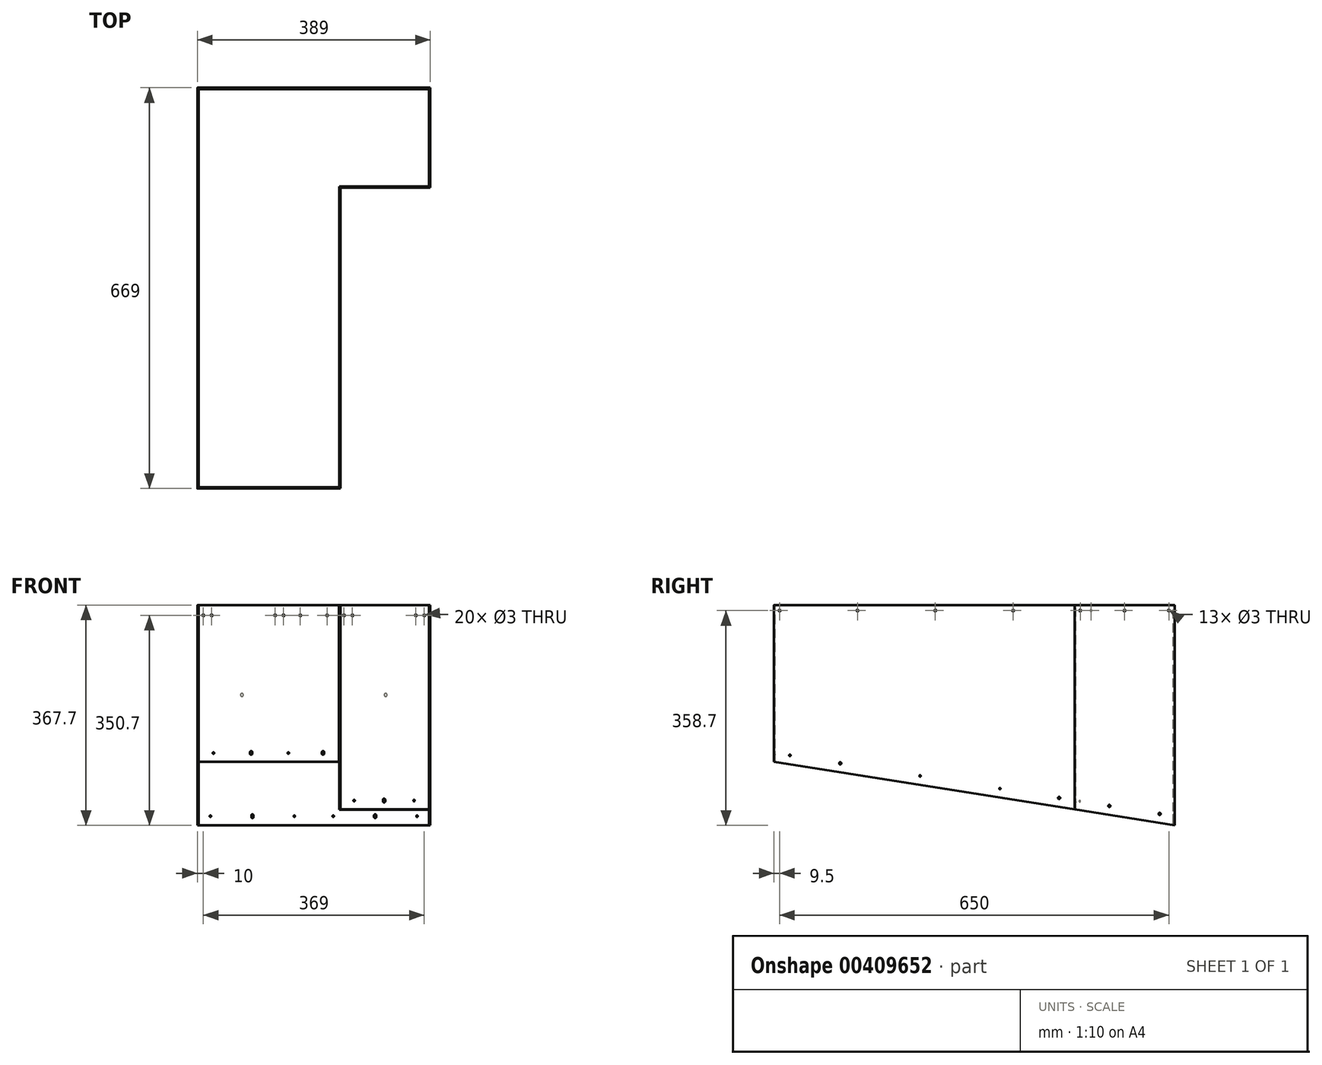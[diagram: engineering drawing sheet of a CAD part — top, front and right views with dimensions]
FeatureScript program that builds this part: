
annotation { "Feature Type Name" : "Feature", "Feature Type Description" : "" }
export const myFeature = defineFeature(function(context is Context, id is Id, definition is map)
    precondition{}
    {
        {
            var Q0;
            Q0=qCreatedBy(makeId("Top.planeOp"),FACE);
            var sketch = newSketch(context, id + "F0", { "sketchPlane" : qUnion([Q0])});
            skLineSegment(sketch, "E0.bottom", {"start": v(192.25, 332.5) * mm, "end": v(-192.25, 332.5) * mm});
            skLineSegment(sketch, "E0.top", {"start": v(192.25, 334.5) * mm, "end": v(-192.25, 334.5) * mm});
            skLineSegment(sketch, "E0.left", {"start": v(192.25, 332.5) * mm, "end": v(192.25, 334.5) * mm});
            skLineSegment(sketch, "E0.right", {"start": v(-192.25, 332.5) * mm, "end": v(-192.25, 334.5) * mm});
            skPoint(sketch, "E0.middle", {"position": v(0, 333.5) * mm});
            skSolve(sketch);
        }
        {
            var Q0;
            Q0 = qSketchRegion(id + "F0", true);
            extrude(context, id + "F1", {"entities" : qUnion([Q0]), "oppositeDirection" : true, "depth" : 367.4 * mm});
        }
        {
            var Q0;
            Q0=qCreatedBy(makeId("Top.planeOp"),FACE);
            var sketch = newSketch(context, id + "F2", { "sketchPlane" : qUnion([Q0])});
            skLineSegment(sketch, "E1.bottom", {"start": v(-192.25, -332.5) * mm, "end": v(42.25, -332.5) * mm});
            skLineSegment(sketch, "E1.top", {"start": v(-192.25, -334.5) * mm, "end": v(42.25, -334.5) * mm});
            skLineSegment(sketch, "E1.left", {"start": v(-192.25, -332.5) * mm, "end": v(-192.25, -334.5) * mm});
            skLineSegment(sketch, "E1.right", {"start": v(42.25, -332.5) * mm, "end": v(42.25, -334.5) * mm});
            skSolve(sketch);
        }
        {
            var Q0;
            Q0 = qSketchRegion(id + "F2", true);
            extrude(context, id + "F3", {"entities" : qUnion([Q0]), "oppositeDirection" : true, "depth" : 261.8 * mm});
        }
        {
            var Q0;
            Q0=qCreatedBy(makeId("Top.planeOp"),FACE);
            var sketch = newSketch(context, id + "F4", { "sketchPlane" : qUnion([Q0])});
            skLineSegment(sketch, "E2.bottom", {"start": v(42.75, 169.5) * mm, "end": v(192.25, 169.5) * mm});
            skLineSegment(sketch, "E2.top", {"start": v(42.75, 167.5) * mm, "end": v(192.25, 167.5) * mm});
            skLineSegment(sketch, "E2.left", {"start": v(42.75, 169.5) * mm, "end": v(42.75, 167.5) * mm});
            skLineSegment(sketch, "E2.right", {"start": v(192.25, 169.5) * mm, "end": v(192.25, 167.5) * mm});
            skSolve(sketch);
        }
        {
            var Q0;
            Q0 = qSketchRegion(id + "F4", true);
            extrude(context, id + "F5", {"entities" : qUnion([Q0]), "oppositeDirection" : true, "depth" : 341.3 * mm});
        }
        {
            var Q0;
            Q0=qCreatedBy(makeId("Top.planeOp"),FACE);
            var sketch = newSketch(context, id + "F6", { "sketchPlane" : qUnion([Q0])});
            skLineSegment(sketch, "E3.bottom", {"start": v(-192.5, -334.5) * mm, "end": v(-194.5, -334.5) * mm});
            skLineSegment(sketch, "E3.top", {"start": v(-192.5, 334.5) * mm, "end": v(-194.5, 334.5) * mm});
            skLineSegment(sketch, "E3.left", {"start": v(-192.5, -334.5) * mm, "end": v(-192.5, 334.5) * mm});
            skLineSegment(sketch, "E3.right", {"start": v(-194.5, -334.5) * mm, "end": v(-194.5, 334.5) * mm});
            skPoint(sketch, "E3.middle", {"position": v(-193.5, 0) * mm});
            skLineSegment(sketch, "E4.bottom", {"start": v(42.5, 167.5) * mm, "end": v(44.5, 167.5) * mm});
            skLineSegment(sketch, "E4.top", {"start": v(42.5, -334.5) * mm, "end": v(44.5, -334.5) * mm});
            skLineSegment(sketch, "E4.left", {"start": v(42.5, 167.5) * mm, "end": v(42.5, -334.5) * mm});
            skLineSegment(sketch, "E4.right", {"start": v(44.5, 167.5) * mm, "end": v(44.5, -334.5) * mm});
            skLineSegment(sketch, "E5.bottom", {"start": v(192.5, 334.5) * mm, "end": v(194.5, 334.5) * mm});
            skLineSegment(sketch, "E5.top", {"start": v(192.5, 167.5) * mm, "end": v(194.5, 167.5) * mm});
            skLineSegment(sketch, "E5.left", {"start": v(192.5, 334.5) * mm, "end": v(192.5, 167.5) * mm});
            skLineSegment(sketch, "E5.right", {"start": v(194.5, 334.5) * mm, "end": v(194.5, 167.5) * mm});
            skSolve(sketch);
        }
        {
            var Q0;
            Q0 = qSketchRegion(id + "F6", true);
            extrude(context, id + "F7", {"entities" : qUnion([Q0]), "oppositeDirection" : true, "depth" : 388 * mm});
        }
        {
            var Q0;
            Q0=makeQuery(id+"F1.opExtrude","SWEPT_FACE",FACE,{"disambiguationData":[OSD([sQuery(id+"F0.wireOp",EDGE,"E0.top")])]});
            var sketch = newSketch(context, id + "F8", { "sketchPlane" : qUnion([Q0])});
            skCircle(sketch, "E6", {"center": v(184.5, -17) * mm, "radius": 1.5 * mm});
            skCircle(sketch, "E7", {"center": v(170.5, -17) * mm, "radius": 1.5 * mm});
            skCircle(sketch, "E8", {"center": v(64.5, -17) * mm, "radius": 1.5 * mm});
            skCircle(sketch, "E9", {"center": v(50.5, -17) * mm, "radius": 1.5 * mm});
            skCircle(sketch, "E10.1.0.0", {"center": v(-64.5, -17) * mm, "radius": 1.5 * mm});
            skCircle(sketch, "E10.1.0.1", {"center": v(-50.5, -17) * mm, "radius": 1.5 * mm});
            skCircle(sketch, "E10.1.0.2", {"center": v(-184.5, -17) * mm, "radius": 1.5 * mm});
            skCircle(sketch, "E10.1.0.3", {"center": v(-170.5, -17) * mm, "radius": 1.5 * mm});
            skLineSegment(sketch, "E10.direction1", {"start": v(50.5, -17) * mm, "end": v(-184.5, -17) * mm, "construction": true});
            skCircle(sketch, "E11", {"center": v(22.5, -17) * mm, "radius": 1.5 * mm});
            skCircle(sketch, "E12", {"center": v(-22.3, -17) * mm, "radius": 1.5 * mm});
            skLineSegment(sketch, "E13", {"start": v(42.5, 7.75) * mm, "end": v(42.5, -58.99) * mm, "construction": true});
            skCircle(sketch, "E14", {"center": v(102.5, -352.4) * mm, "radius": 1.75 * mm, "construction": true});
            skCircle(sketch, "E15", {"center": v(-102.5, -352.4) * mm, "radius": 1.75 * mm, "construction": true});
            skCircle(sketch, "E16", {"center": v(172.5, -352.4) * mm, "radius": 1.2 * mm});
            skCircle(sketch, "E17", {"center": v(-172.5, -352.4) * mm, "radius": 1.2 * mm});
            skCircle(sketch, "E18", {"center": v(-32.5, -352.4) * mm, "radius": 1.2 * mm});
            skCircle(sketch, "E19", {"center": v(32.5, -352.4) * mm, "radius": 1.2 * mm});
            skLineSegment(sketch, "E20.left", {"start": v(-100.75, -354.4) * mm, "end": v(-100.75, -350.4) * mm});
            skLineSegment(sketch, "E20.right", {"start": v(-104.25, -354.4) * mm, "end": v(-104.25, -350.4) * mm});
            skArc(sketch, "E21", {"start": v(-100.75, -350.4) * mm, "mid": v(-102.5, -349.37) * mm, "end": v(-104.25, -350.4) * mm});
            skArc(sketch, "E22", {"start": v(-104.25, -354.4) * mm, "mid": v(-102.5, -355.43) * mm, "end": v(-100.75, -354.4) * mm});
            skLineSegment(sketch, "E23.left", {"start": v(104.25, -354.4) * mm, "end": v(104.25, -350.4) * mm});
            skLineSegment(sketch, "E23.right", {"start": v(100.75, -354.4) * mm, "end": v(100.75, -350.4) * mm});
            skArc(sketch, "E24", {"start": v(104.25, -350.4) * mm, "mid": v(102.5, -349.37) * mm, "end": v(100.75, -350.4) * mm});
            skArc(sketch, "E25", {"start": v(100.75, -354.4) * mm, "mid": v(102.5, -355.43) * mm, "end": v(104.25, -354.4) * mm});
            skLineSegment(sketch, "E26", {"start": v(-192.5, 1.16) * mm, "end": v(192.5, 1.16) * mm, "construction": true});
            skCircle(sketch, "E27", {"center": v(-120, -150) * mm, "radius": 2.5 * mm});
            skCircle(sketch, "E28", {"center": v(120, -150) * mm, "radius": 2.5 * mm});
            skSolve(sketch);
        }
        {
            var Q0;
            Q0 = qSketchRegion(id + "F8", true);
            extrude(context, id + "F9", {"entities" : qUnion([Q0]), "operationType" : NewBodyOperationType.REMOVE, "oppositeDirection" : true, "depth" : 2 * mm});
        }
        {
            var Q0;
            Q0=makeQuery(id+"F3.opExtrude","SWEPT_FACE",FACE,{"disambiguationData":[OSD([sQuery(id+"F2.wireOp",EDGE,"E1.top")])]});
            var sketch = newSketch(context, id + "F10", { "sketchPlane" : qUnion([Q0])});
            skCircle(sketch, "E29", {"center": v(-184.5, -17) * mm, "radius": 1.5 * mm});
            skCircle(sketch, "E30", {"center": v(-170.5, -17) * mm, "radius": 1.5 * mm});
            skCircle(sketch, "E31.1.0.0", {"center": v(-64.5, -17) * mm, "radius": 1.5 * mm});
            skCircle(sketch, "E31.1.0.1", {"center": v(-50.5, -17) * mm, "radius": 1.5 * mm});
            skCircle(sketch, "E32.1.0.0", {"center": v(-22.5, -17) * mm, "radius": 1.5 * mm});
            skCircle(sketch, "E32.1.0.1", {"center": v(22.3, -17) * mm, "radius": 1.5 * mm});
            skCircle(sketch, "E33", {"center": v(-104.5, -246.8) * mm, "radius": 1.75 * mm, "construction": true});
            skCircle(sketch, "E34", {"center": v(15.5, -246.8) * mm, "radius": 1.75 * mm, "construction": true});
            skCircle(sketch, "E35", {"center": v(-167.5, -246.8) * mm, "radius": 1.2 * mm});
            skCircle(sketch, "E36", {"center": v(-42.5, -246.8) * mm, "radius": 1.2 * mm});
            skLineSegment(sketch, "E37.left", {"start": v(-102.75, -248.8) * mm, "end": v(-102.75, -244.8) * mm});
            skLineSegment(sketch, "E37.right", {"start": v(-106.25, -248.8) * mm, "end": v(-106.25, -244.8) * mm});
            skArc(sketch, "E38", {"start": v(-102.75, -244.8) * mm, "mid": v(-104.5, -243.77) * mm, "end": v(-106.25, -244.8) * mm});
            skArc(sketch, "E39", {"start": v(-106.25, -248.8) * mm, "mid": v(-104.5, -249.83) * mm, "end": v(-102.75, -248.8) * mm});
            skLineSegment(sketch, "E40.left", {"start": v(17.25, -248.8) * mm, "end": v(17.25, -244.8) * mm});
            skLineSegment(sketch, "E40.right", {"start": v(13.75, -248.8) * mm, "end": v(13.75, -244.8) * mm});
            skArc(sketch, "E41", {"start": v(17.25, -244.8) * mm, "mid": v(15.5, -243.77) * mm, "end": v(13.75, -244.8) * mm});
            skArc(sketch, "E42", {"start": v(13.75, -248.8) * mm, "mid": v(15.5, -249.83) * mm, "end": v(17.25, -248.8) * mm});
            skLineSegment(sketch, "E43", {"start": v(-192.5, 3.66) * mm, "end": v(42.5, 3.66) * mm, "construction": true});
            skSolve(sketch);
        }
        {
            var Q0;
            Q0 = qSketchRegion(id + "F10", true);
            extrude(context, id + "F11", {"entities" : qUnion([Q0]), "operationType" : NewBodyOperationType.REMOVE, "oppositeDirection" : true, "depth" : 2 * mm});
        }
        {
            var Q0;
            Q0=makeQuery(id+"F7.opExtrude","SWEPT_FACE",FACE,{"disambiguationData":[OSD([sQuery(id+"F6.wireOp",EDGE,"E3.right")])]});
            var sketch = newSketch(context, id + "F12", { "sketchPlane" : qUnion([Q0])});
            skCircle(sketch, "E44", {"center": v(-325, -9) * mm, "radius": 1.5 * mm});
            skLineSegment(sketch, "E45", {"start": v(-334.5, -367.7) * mm, "end": v(334.5, -367.7) * mm});
            skLineSegment(sketch, "E46", {"start": v(-334.5, -367.7) * mm, "end": v(334.5, -261.74) * mm});
            skLineSegment(sketch, "E47", {"start": v(334.5, -261.74) * mm, "end": v(334.5, -367.7) * mm});
            skLineSegment(sketch, "E48", {"start": v(-334.5, -367.7) * mm, "end": v(-334.5, -388) * mm});
            skLineSegment(sketch, "E49", {"start": v(-334.5, -388) * mm, "end": v(334.5, -388) * mm});
            skLineSegment(sketch, "E50", {"start": v(334.5, -388) * mm, "end": v(334.5, -367.7) * mm});
            skCircle(sketch, "E51.1.0.0", {"center": v(-195, -9) * mm, "radius": 1.5 * mm});
            skCircle(sketch, "E51.2.0.0", {"center": v(-65, -9) * mm, "radius": 1.5 * mm});
            skCircle(sketch, "E51.3.0.0", {"center": v(65, -9) * mm, "radius": 1.5 * mm});
            skCircle(sketch, "E51.4.0.0", {"center": v(195, -9) * mm, "radius": 1.5 * mm});
            skCircle(sketch, "E51.5.0.0", {"center": v(325, -9) * mm, "radius": 1.5 * mm});
            skLineSegment(sketch, "E51.direction1", {"start": v(-325, -9) * mm, "end": v(-195, -9) * mm, "construction": true});
            skCircle(sketch, "E52", {"center": v(-309.59, -348.57) * mm, "radius": 1.75 * mm});
            skLineSegment(sketch, "E53", {"start": v(-334.5, -367.7) * mm, "end": v(-337.36, -349.64) * mm, "construction": true});
            skCircle(sketch, "E54", {"center": v(223.77, -264.1) * mm, "radius": 1.75 * mm});
            skCircle(sketch, "E55.1.0.0", {"center": v(-176.25, -327.45) * mm, "radius": 1.75 * mm, "construction": true});
            skCircle(sketch, "E55.2.0.0", {"center": v(-42.91, -306.33) * mm, "radius": 1.75 * mm, "construction": true});
            skLineSegment(sketch, "E55.direction1", {"start": v(-309.59, -348.57) * mm, "end": v(-176.25, -327.45) * mm, "construction": true});
            skCircle(sketch, "E56.0.3.0", {"center": v(90.43, -285.21) * mm, "radius": 1.75 * mm, "construction": true});
            skCircle(sketch, "E57", {"center": v(307.72, -250.8) * mm, "radius": 1.2 * mm});
            skCircle(sketch, "E58", {"center": v(-176.25, -327.45) * mm, "radius": 1.2 * mm});
            skCircle(sketch, "E59", {"center": v(-42.91, -306.33) * mm, "radius": 1.2 * mm});
            skCircle(sketch, "E60", {"center": v(90.43, -285.21) * mm, "radius": 1.2 * mm});
            skSolve(sketch);
        }
        {
            var Q0;
            Q0 = qSketchRegion(id + "F12", true);
            extrude(context, id + "F13", {"entities" : qUnion([Q0]), "operationType" : NewBodyOperationType.REMOVE, "oppositeDirection" : true, "depth" : 2 * mm});
        }
        {
            var Q0;
            Q0=makeQuery(id+"F12.imprint","IMPRINT",FACE,{"disambiguationData":[TD([[makeQuery(id+"F12.imprint","IMPRINT",EDGE,{"derivedFrom":sQuery(id+"F12.wireOp",EDGE,"E45")}),-1.0]])]});
            var Q1;
            Q1=makeQuery(id+"F12.imprint","IMPRINT",FACE,{"disambiguationData":[TD([[makeQuery(id+"F12.imprint","IMPRINT",EDGE,{"derivedFrom":sQuery(id+"F12.wireOp",EDGE,"E45")}),1.0]])]});
            extrude(context, id + "F14", {"entities" : qUnion([Q0, Q1]), "operationType" : NewBodyOperationType.REMOVE, "oppositeDirection" : true, "depth" : 428 * mm});
        }
        {
            var Q0;
            Q0=makeQuery(id+"F7.opExtrude","SWEPT_FACE",FACE,{"disambiguationData":[OSD([sQuery(id+"F6.wireOp",EDGE,"E5.right")])]});
            var sketch = newSketch(context, id + "F15", { "sketchPlane" : qUnion([Q0])});
            skCircle(sketch, "E61", {"center": v(325, -9) * mm, "radius": 1.5 * mm});
            skCircle(sketch, "E62.1.0.0", {"center": v(251, -9) * mm, "radius": 1.5 * mm});
            skCircle(sketch, "E62.2.0.0", {"center": v(177, -9) * mm, "radius": 1.5 * mm});
            skLineSegment(sketch, "E62.direction1", {"start": v(325, -9) * mm, "end": v(251, -9) * mm, "construction": true});
            skCircle(sketch, "E63", {"center": v(309.59, -348.57) * mm, "radius": 1.75 * mm});
            skCircle(sketch, "E64", {"center": v(225.63, -335.27) * mm, "radius": 1.75 * mm});
            skSolve(sketch);
        }
        {
            var Q0;
            Q0 = qSketchRegion(id + "F15", true);
            extrude(context, id + "F16", {"entities" : qUnion([Q0]), "operationType" : NewBodyOperationType.REMOVE, "oppositeDirection" : true, "depth" : 2 * mm});
        }
        {
            var Q0;
            Q0=makeQuery(id+"F5.opExtrude","SWEPT_FACE",FACE,{"disambiguationData":[OSD([sQuery(id+"F4.wireOp",EDGE,"E2.top")])]});
            var sketch = newSketch(context, id + "F17", { "sketchPlane" : qUnion([Q0])});
            skCircle(sketch, "E65", {"center": v(50.5, -17) * mm, "radius": 1.5 * mm});
            skCircle(sketch, "E66", {"center": v(64.5, -17) * mm, "radius": 1.5 * mm});
            skCircle(sketch, "E67", {"center": v(170.5, -17) * mm, "radius": 1.5 * mm});
            skCircle(sketch, "E68", {"center": v(184.5, -17) * mm, "radius": 1.5 * mm});
            skCircle(sketch, "E69", {"center": v(117.5, -326.3) * mm, "radius": 1.75 * mm, "construction": true});
            skCircle(sketch, "E70", {"center": v(67.5, -326.3) * mm, "radius": 1.2 * mm});
            skCircle(sketch, "E71", {"center": v(167.5, -326.3) * mm, "radius": 1.2 * mm});
            skLineSegment(sketch, "E72.left", {"start": v(119.25, -328.3) * mm, "end": v(119.25, -324.3) * mm});
            skLineSegment(sketch, "E72.right", {"start": v(115.75, -328.3) * mm, "end": v(115.75, -324.3) * mm});
            skArc(sketch, "E73", {"start": v(119.25, -324.3) * mm, "mid": v(117.5, -323.27) * mm, "end": v(115.75, -324.3) * mm});
            skArc(sketch, "E74", {"start": v(115.75, -328.3) * mm, "mid": v(117.5, -329.33) * mm, "end": v(119.25, -328.3) * mm});
            skSolve(sketch);
        }
        {
            var Q0;
            Q0 = qSketchRegion(id + "F17", true);
            extrude(context, id + "F18", {"entities" : qUnion([Q0]), "operationType" : NewBodyOperationType.REMOVE, "oppositeDirection" : true, "depth" : 2 * mm});
        }
        {
            var Q0;
            Q0=makeQuery(id+"F7.opExtrude","SWEPT_FACE",FACE,{"disambiguationData":[OSD([sQuery(id+"F6.wireOp",EDGE,"E4.right")])]});
            var sketch = newSketch(context, id + "F19", { "sketchPlane" : qUnion([Q0])});
            skCircle(sketch, "E75", {"center": v(-325, -9) * mm, "radius": 1.5 * mm});
            skCircle(sketch, "E76.1.0.0", {"center": v(-195, -9) * mm, "radius": 1.5 * mm});
            skCircle(sketch, "E76.2.0.0", {"center": v(-65, -9) * mm, "radius": 1.5 * mm});
            skCircle(sketch, "E76.3.0.0", {"center": v(65, -9) * mm, "radius": 1.5 * mm});
            skCircle(sketch, "E76.4.0.0", {"center": v(195, -9) * mm, "radius": 1.5 * mm});
            skCircle(sketch, "E76.5.0.0", {"center": v(325, -9) * mm, "radius": 1.5 * mm});
            skLineSegment(sketch, "E76.direction1", {"start": v(-325, -9) * mm, "end": v(-195, -9) * mm, "construction": true});
            skPoint(sketch, "E77.0", {"position": v(-307.72, -250.8) * mm});
            skPoint(sketch, "E77.1", {"position": v(-223.77, -264.1) * mm});
            skPoint(sketch, "E77.2", {"position": v(-90.43, -285.21) * mm});
            skCircle(sketch, "E78", {"center": v(-223.77, -264.1) * mm, "radius": 1.75 * mm});
            skCircle(sketch, "E79", {"center": v(-307.72, -250.8) * mm, "radius": 1.2 * mm});
            skCircle(sketch, "E80", {"center": v(-90.43, -285.21) * mm, "radius": 1.2 * mm});
            skPoint(sketch, "E81.0", {"position": v(42.91, -306.33) * mm});
            skCircle(sketch, "E82", {"center": v(42.91, -306.33) * mm, "radius": 1.2 * mm});
            skCircle(sketch, "E83", {"center": v(141.68, -321.97) * mm, "radius": 1.75 * mm});
            skSolve(sketch);
        }
        {
            var Q0;
            Q0 = qSketchRegion(id + "F19", true);
            extrude(context, id + "F20", {"entities" : qUnion([Q0]), "operationType" : NewBodyOperationType.REMOVE, "oppositeDirection" : true, "depth" : 2 * mm});
        }
        {
            var Q0;
            Q0=makeQuery(id+"F7.opExtrude","CAP_EDGE",EDGE,{"disambiguationData":[OSD([sQuery(id+"F6.wireOp",EDGE,"E3.top")])],"isStart":true});
            var Q1;
            Q1=makeQuery(id+"F7.opExtrude","CAP_EDGE",EDGE,{"disambiguationData":[OSD([sQuery(id+"F6.wireOp",EDGE,"E3.bottom")])],"isStart":true});
            var Q2;
            Q2=makeQuery(id+"F7.opExtrude","CAP_EDGE",EDGE,{"disambiguationData":[OSD([sQuery(id+"F6.wireOp",EDGE,"E5.bottom")])],"isStart":true});
            var Q3;
            Q3=makeQuery(id+"F7.opExtrude","CAP_EDGE",EDGE,{"disambiguationData":[OSD([sQuery(id+"F6.wireOp",EDGE,"E5.top")])],"isStart":true});
            var Q4;
            Q4=makeQuery(id+"F5.opExtrude","CAP_EDGE",EDGE,{"disambiguationData":[OSD([sQuery(id+"F4.wireOp",EDGE,"E2.right")])],"isStart":true});
            var Q5;
            Q5=makeQuery(id+"F5.opExtrude","CAP_EDGE",EDGE,{"disambiguationData":[OSD([sQuery(id+"F4.wireOp",EDGE,"E2.left")])],"isStart":true});
            var Q6;
            Q6=makeQuery(id+"F1.opExtrude","CAP_EDGE",EDGE,{"disambiguationData":[OSD([sQuery(id+"F0.wireOp",EDGE,"E0.left")])],"isStart":true});
            var Q7;
            Q7=makeQuery(id+"F1.opExtrude","CAP_EDGE",EDGE,{"disambiguationData":[OSD([sQuery(id+"F0.wireOp",EDGE,"E0.right")])],"isStart":true});
            var Q8;
            Q8=makeQuery(id+"F7.opExtrude","CAP_EDGE",EDGE,{"disambiguationData":[OSD([sQuery(id+"F6.wireOp",EDGE,"E4.top")])],"isStart":true});
            var Q9;
            Q9=makeQuery(id+"F7.opExtrude","CAP_EDGE",EDGE,{"disambiguationData":[OSD([sQuery(id+"F6.wireOp",EDGE,"E4.bottom")])],"isStart":true});
            var Q10;
            Q10=makeQuery(id+"F3.opExtrude","CAP_EDGE",EDGE,{"disambiguationData":[OSD([sQuery(id+"F2.wireOp",EDGE,"E1.right")])],"isStart":true});
            var Q11;
            Q11=makeQuery(id+"F3.opExtrude","CAP_EDGE",EDGE,{"disambiguationData":[OSD([sQuery(id+"F2.wireOp",EDGE,"E1.left")])],"isStart":true});
            fillet(context, id + "F21", {"entities" : qUnion([Q0, Q1, Q2, Q3, Q4, Q5, Q6, Q7, Q8, Q9, Q10, Q11]), "radius" : 1 * mm, "tangentPropagation" : true, "allowEdgeOverflow" : false});
        }
    });
